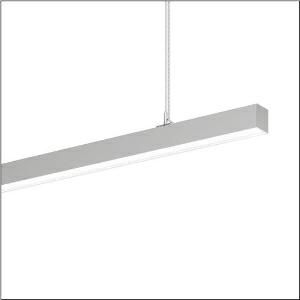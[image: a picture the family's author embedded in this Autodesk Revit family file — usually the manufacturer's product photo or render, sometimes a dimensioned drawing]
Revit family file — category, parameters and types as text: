
# Revit family: silica_r__21_51mx33db39sb_b1fc
name_source: partatom
category: Lighting Fixtures
units: mm (PartAtom-declared; Revit-internal decimal feet)

## family parameters
Cut with Voids When Loaded = No
Host = Face
Light Source = No
Part Type = Normal
Room Calculation Point = No
Round Connector Dimension = Use Diameter
Shared = No

## types (1)
- --- (1 x LED, 7390 lm, 51.6 W, 3000K)
    Apparent Load = 52 VA
    CIE Flux Codes = 78 96 99 55 100
    Color Rendering = 80
    Color Temperature = 3000K
    Default Elevation = 1800 mm
    Description = Silica® 21, office luminaire, primary optical cover: prismatic diffuser, of PMMA, CAT 2 (L<= 3000cd/m²), light emission: direct/indirect distribution, primary light characteristic: symmetric, installation type: suspended mounting, LED, rated luminous flux: 7.390lm, luminous efficacy: 143lm/W, light colour: 830, colour temperature: 3000K, with terminal, 3+2-pole, max. 2.5mm², mains connection: 220..240V, AC, 50/60Hz, rated input power: 51.6W, luminaire housing, of aluminium, metallic grey (RAL 9006), length: 1.504mm, width: 53mm, height: 53mm, protection rating (complete): IP20, insulation class (complete): insulation class I (protective earthing), certification: CE, permissible operating ambient temperature: 0..+35°C, standard: EN 50419, packaging unit: 1 piece
    Height = 53 mm
    Lamp = 1 x LED
    Lamp Light Flux = 7390 lm
    Lamp Power = 51.6 W
    Lamp count = 1
    Length = 1504 mm
    Luminous efficacy = 143 lm/W
    Manufacturer = Siteco
    ModVariant = No
    Model = 51MX33DB39SB
    Mounting Place = Ceiling
    Mounting Type = Pendant
    Number of Poles = 1
    OnlyDefault = Yes
    Power Factor = 1
    Product Name = Silica® 21
    Product group = office luminaire | ceiling pendant
    ProductGroupID = 902
    Protection Class = Protection class I
    Protection Degree = IP 20
    RLX_Detail_Level = 1
    RLX_Emergency_Light_Flux = 0 lm
    RLX_Emergency_Type = 0
    RLX_Emergency_Type_DB = No
    RlxData = <blob elided: 23477 chars, md5=933749a9>
    Socket = socket
    Standby Power = 0 W
    System Light Flux = 7390 lm
    System Power = 52 W
    Type Comments = factory setting: luminous flux: 100 % | dim-lin: 254 | 345 mA
    Type Image = l_1297747.jpg
    URL = http://relux.com
    VarID = @adj_048653
    Voltage = 0 V
    Weight = 0.00 kg
    Width = 53 mm

## geometry (parser evidence)
native form markers: Blend x4, Sweep x11
no freeform markers — native parametric forms only
